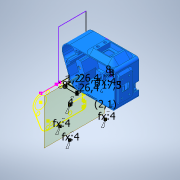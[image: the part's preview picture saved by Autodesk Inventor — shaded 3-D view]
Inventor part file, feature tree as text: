
AUTODESK INVENTOR PART (.ipt)
format: ipt  version: 2021.1 (Build 251245010, 245A)  size: 1,963,008 bytes
history: mixed  units: in
note: dims shown in document units (in); Inventor stores cm internally (conversion verified against a paired STEP export)
features: extrude x24, sketch x21, move_body x9, direct_edit x7, chamfer x6, projected_geometry x5, other x4, revolve x3, fillet x1, plane x1, imported_body x1
ambient origin geometry x8: Origin, YZ Plane, XZ Plane, XY Plane, X Axis, Y Axis, Z Axis, Center Point
bodies: Solid1 (imported_parasolid), Volumenkörper268 (imported_parasolid), Body1 (imported_parasolid)
feature tree (82):
  sketch  "Skizze1"  dims[d0=0.1575in d1=0.1575in]
  extrude  "Extrusion2"  Depth=0.1575in
  extrude  "Extrusion1"  Depth=0.1575in
  sketch  "Skizze3"  dims[d2=0.1575in d3=0.1575in]
  extrude  "Extrusion3"  Depth=0.252in TaperAngle=0.0deg
  extrude  "Extrusion4"  Depth=0.2756in TaperAngle=0.0deg
  extrude  "Extrusion5"  Depth=0.1575in
  extrude  "Extrusion6"  Depth=0.1575in
  direct_edit  "Direktbearbeitung2"
  extrude  "Extrusion8"  Depth=0.315in
  direct_edit  "Direktbearbeitung3"
  extrude  "Extrusion10"  Depth=0.1969in TaperAngle=0.0deg
  extrude  "Extrusion11"  TaperAngle=135.0deg  [1 undecoded]
  sketch  "Skizze16"  dims[d19=45.0deg d20=0.1969in d21=0.5906in d22=0.0in d23=0.0in]
  direct_edit  "Direktbearbeitung4"
  extrude  "Extrusion19"  TaperAngle=0.0deg  [1 undecoded]
  direct_edit  "Direktbearbeitung6"
  direct_edit  "Direktbearbeitung7"
  chamfer  "Fase2"  Distance=0.0157in
  extrude  "Extrusion26"  TaperAngle=135.0deg  [1 undecoded]
  chamfer  "Fase4"  Distance=0.3937in
  sketch  "Skizze29"  dims[d32=0.3937in d33=0.2362in d34=0.0in d35=0.0in d36=0.0in d37=0.0in d38=-0.0394in d39=0.0157in d40=0.0in]
  extrude  "Extrusion30"  TaperAngle=0.0deg  [1 undecoded]
  extrude  "Extrusion35"  Depth=0.3937in
  other  "Flächenverjüngung3"
  extrude  "Extrusion36"  Depth=0.315in
  revolve  "Umdrehung1"
  sketch  "Skizze36"  dims[d45=0.3937in d46=0.0in d69=0.0in d70=0.0in d71=-0.2756in]
  fillet  "Rundung3"  Radius=0.315in
  extrude  "Extrusion37"  Depth=0.1181in TaperAngle=0.0deg
  chamfer  "Fase5"  [1 undecoded]
  plane  "Arbeitsebene2"
  extrude  "Extrusion38"  Depth=0.0787in
  extrude  "Extrusion39"  Depth=0.0197in
  extrude  "Extrusion40"  Depth=0.0787in TaperAngle=45.0deg
  chamfer  "Fase6"  Distance=0.0197in
  extrude  "Extrusion41"  Depth=0.1181in
  chamfer  "Fase7"  Distance=0.0197in
  extrude  "Extrusion42"  TaperAngle=90.0deg  [1 undecoded]
  extrude  "Extrusion9"  Depth=0.0787in
  direct_edit  "Direktbearbeitung8"
  sketch  "Skizze44"  dims[d122=0.0157in d123=0.0in d124=0.0197in d125=0.0787in d126=45.0deg d133=0.0197in d134=0.0in]
  sketch  "Skizze45"  dims[d144=0.3346in d145=0.0in d147=0.1181in]
  direct_edit  "Direktbearbeitung10"
  sketch  "Skizze47"  dims[d148=45.0deg d149=0.0197in d150=0.0in]
  extrude  "Extrusion43"  Depth=0.0787in TaperAngle=0.0deg
  extrude  "Extrusion44"  Depth=0.0787in TaperAngle=45.0deg
  chamfer  "Fase8"  Distance=0.3937in
  extrude  "Extrusion45"  Depth=0.0787in
  projected_geometry  "Projizierte Kontur2"
  sketch  "Skizze4"  dims[d4=0.1575in d5=0.252in d6=0.0in]
  sketch  "Skizze5"  dims[d7=0.2362in d8=0.0in d9=0.2756in d10=0.0in]
  sketch  "Skizze8"  dims[d11=0.1575in d12=0.0in d13=0.1575in]
  sketch  "Skizze9"  dims[d14=0.1575in d15=0.1575in]
  sketch  "Skizze10"  dims[d16=0.252in d17=0.0in d18=0.315in]
  sketch  "Skizze26"  dims[d30=0.315in d31=135.0deg]
  sketch  "Skizze35"  dims[d41=0.315in d42=135.0deg d43=0.3937in d44=0.0in]
  sketch  "Skizze37"  dims[d72=0.3937in d73=0.0in d74=1.0394in]
  projected_geometry  "Projizierte Kontur7"
  sketch  "Skizze38"  dims[d75=1.0394in d76=0.0472in d86=0.315in]
  sketch  "Skizze39"  dims[d87=0.2362in d88=0.0in d89=0.0in d90=0.1181in d104=0.0in d105=0.0in d106=-0.0787in]
  projected_geometry  "Projizierte Kontur8"
  sketch  "Skizze40"  dims[d109=0.0197in d113=0.0197in d114=0.0787in d115=45.0deg d119=0.0197in]
  projected_geometry  "Projizierte Kontur9"
  sketch  "Skizze41"  dims[d120=0.0197in d121=0.0197in]
  sketch  "Skizze48"  dims[d151=0.1969in d152=90.0deg d153=0.0787in d154=0.0787in d155=0.0in d156=0.0787in d157=0.0787in d158=45.0deg d159=0.3937in d160=0.0787in d161=1.9685in d162=0.0in d163=0.1969in d164=0.1969in d165=135.0deg d166=0.0394in d167=0.0in d168=0.1575in d172=0.1811in d173=0.252in d174=0.0in d175=0.0197in d176=0.0787in d177=45.0deg d178=0.1969in d179=0.1969in d180=0.0394in d181=0.0in d182=0.0197in d183=0.0787in d184=45.0deg d185=0.0157in d186=0.0in d187=-0.6184in d188=0.0in d189=2.8346in d190=0.0in d191=4.1339in d192=0.0in d193=0.0in d194=0.0in d195=0.0in d196=1.3346in d197=-1.0433in d198=0.0in d199=0.0in d201=180.0deg d202=3.9375in d203=0.1875in d204=0.375in d205=0.1575in d206=0.315in d207=0.3937in d208=0.0in d209=0.1969in d210=0.0354in d211=0.0in d212=0.0197in d213=0.0787in d214=45.0deg d215=0.2362in d216=0.0591in d217=0.0079in d218=0.0in d219=0.689in d220=0.0827in]
  projected_geometry  "Projizierte Kontur11"
  other  "Löschen2"
  other  "Löschen3"
  move_body  "Verschieben1"
  other  "Löschen4"
  move_body  "Verschieben2"
  move_body  "Verschieben4"
  move_body  "Verschieben5"
  revolve  "Drehen1"  [1 undecoded]
  move_body  "Verschieben6"
  move_body  "Verschieben7"
  move_body  "Verschieben8"
  move_body  "Verschieben9"
  revolve  "Drehen3"  [1 undecoded]
  move_body  "Verschieben10"
  imported_body  NMx_Import_Brep_tag  [imported B-rep: ~74 faces, bbox_mm=[106.981267, 80.0, 48.4]]
note: 8 required parameter values undecoded (feature->parameter linkage not recoverable at this tier; creation-order binding heuristic only, values carry confidence <= 0.55)